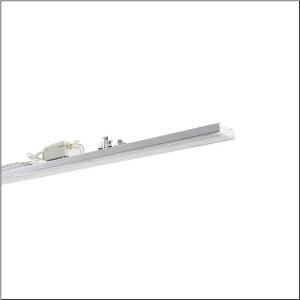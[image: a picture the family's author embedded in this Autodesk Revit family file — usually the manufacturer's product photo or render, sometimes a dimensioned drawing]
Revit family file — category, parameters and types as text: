
# Revit family: licross_r__21_recessed_ho_52tl11de47xs_6da4
name_source: partatom
category: Lighting Fixtures
units: mm (PartAtom-declared; Revit-internal decimal feet)

## family parameters
Cut with Voids When Loaded = No
Host = Face
Light Source = No
Part Type = Normal
Room Calculation Point = No
Round Connector Dimension = Use Diameter
Shared = No

## types (1)
- --- (1 x LED, 7480 lm, 44.1 W, 4000K)
    Apparent Load = 44 VA
    CIE Flux Codes = 87 95 99 100 100
    Color Rendering = 80
    Color Temperature = 4000K
    Default Elevation = 1800 mm
    Description = Licross® 21 Recessed HO, luminaire insert, of sheet steel, galvanised, coil coated, white, length: 750mm, width: 66mm, height: 67mm, LED rated luminous flux: 7.480lm, light colour: 840, control gear: DALI 2, with plug, 5-pole, with phase selection, mains connection: 220..240V, AC, 50/60Hz, rated input power: 44W, halogen-free wiring, primary light control with lens, of plastic, primary optical cover: cover, of PMMA, light emission: direct distribution, primary light characteristic: symmetric, protection rating (complete): IP40, insulation class (complete): insulation class I (protective earthing), certification: CE, ENEC, VDE, UKCA, protection symbol: D if used in an environment without relevant dust loads with corresponding accessories, impact resistance: IK06, permissible ambient temperature for indoor applications: -25..+30°C, corresponds to IFS (International Featured Standards) requirements for safety and quality in the food industry, reducing of maximum allowable ambient temperature of 5°C with ceiling mounting, LABS conformity tested according to VDMA 24364:2018-05, packaging unit: 1 piece
    Height = 58 mm
    Lamp = 1 x LED
    Lamp Light Flux = 7480 lm
    Lamp Power = 44.1 W
    Lamp count = 1
    Length = 750 mm
    Luminous efficacy = 170 lm/W
    Manufacturer = Siteco
    ModVariant = No
    Model = 52TL11DE47XS
    Mounting Place = Ceiling
    Mounting Type = Pendant
    Number of Poles = 1
    OnlyDefault = Yes
    Power Factor = 1
    Product Name = Licross® 21 Recessed HO
    Product group = luminaire insert
    ProductGroupID = 901
    Protection Class = Protection class I
    Protection Degree = IP 40
    RLX_Detail_Level = 1
    RLX_Emergency_Light_Flux = 0 lm
    RLX_Emergency_Type = 0
    RLX_Emergency_Type_DB = No
    RlxData = <blob elided: 29289 chars, md5=42ebf60f>
    Socket = socket
    Standby Power = 0 W
    System Light Flux = 7480 lm
    System Power = 44 W
    Type Comments = factory setting: luminous flux: 100 % | dim-lin: 254 | 484 mA
    Type Image = l_1296930.jpg
    URL = http://relux.com
    VarID = @adj_059073
    Voltage = 0 V
    Weight = 0.00 kg
    Width = 66 mm

## geometry (parser evidence)
native form markers: Blend x4, Sweep x11
no freeform markers — native parametric forms only
